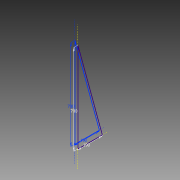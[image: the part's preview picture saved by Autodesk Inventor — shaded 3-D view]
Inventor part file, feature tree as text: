
AUTODESK INVENTOR PART (.ipt)
format: ipt  version: 2015 (Build 190159000, 159)  size: 68,096 bytes
history: native  units: mm
features: sketch x1
ambient origin geometry x8: Origin, YZ Plane, XZ Plane, XY Plane, X Axis, Y Axis, Z Axis, Center Point
feature tree (1):
  sketch  "Sketch1"  dims[d1=700.0mm d4=190.0mm]
